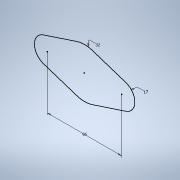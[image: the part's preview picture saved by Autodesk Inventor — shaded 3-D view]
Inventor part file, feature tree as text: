
AUTODESK INVENTOR PART (.ipt)
format: ipt  version: 2021 (Build 250183000, 183)  size: 90,624 bytes
history: native  units: mm
features: sketch x1
ambient origin geometry x8: Origin, YZ Plane, XZ Plane, XY Plane, X Axis, Y Axis, Z Axis, Center Point
feature tree (1):
  sketch  "Esboço1"  dims[d0=32.0mm d1=17.0mm d2=96.0mm]
